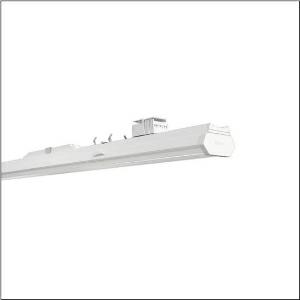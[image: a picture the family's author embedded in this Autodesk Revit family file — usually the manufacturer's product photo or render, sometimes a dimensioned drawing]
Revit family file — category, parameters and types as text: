
# Revit family: licross_r__21_performance_mo_52td16cn445g_c2c6
name_source: partatom
category: Lighting Fixtures
units: mm (PartAtom-declared; Revit-internal decimal feet)

## family parameters
Cut with Voids When Loaded = No
Host = Face
Light Source = No
Part Type = Normal
Room Calculation Point = No
Round Connector Dimension = Use Diameter
Shared = No

## types (1)
- --- (1 x LED, 4500 lm, 24.1 W, 4000K)
    Apparent Load = 24 VA
    CIE Flux Codes = 66 88 96 79 100
    Color Rendering = 80
    Color Temperature = 4000K
    Default Elevation = 1800 mm
    Description = Licross® 21 Performance MO, luminaire insert, of sheet steel, galvanised, coil coated, white, length: 1.500mm, width: 120mm, height: 123mm, LED rated luminous flux: 4.500lm, light colour: 840, control gear: ON/OFF Multilumen, CLOi, control gear: ECG Multilumen, with plug, 3-pole, with phase selection, mains connection: 220..240V, AC, 50/60Hz, halogen-free wiring, primary light control with lens, of plastic, primary optical cover: cover, of PMMA, CAT 2 (L<= 3000cd/m²), light emission: direct/indirect distribution, primary light characteristic: symmetric, protection rating (complete): IP54, insulation class (complete): insulation class I (protective earthing), certification: CE, ENEC, UKCA, protection symbol: D if used in an environment with non-conductive dust loads with corresponding accessories, impact resistance: IK06, permissible ambient temperature for indoor applications: -35..+55°C, corresponds to IFS (International Featured Standards) requirements for safety and quality in the food industry, reducing of maximum allowable ambient temperature of 5°C with ceiling mounting, LABS conformity tested according to VDMA 24364:2018-05, packaging unit: 1 piece
    Height = 114 mm
    Lamp = 1 x LED
    Lamp Light Flux = 4500 lm
    Lamp Power = 24.1 W
    Lamp count = 1
    Length = 1500 mm
    Luminous efficacy = 187 lm/W
    Manufacturer = Siteco
    ModVariant = No
    Model = 52TD16CN445G
    Mounting Place = Ceiling
    Mounting Type = Pendant
    Number of Poles = 1
    OnlyDefault = Yes
    Power Factor = 1
    Product Name = Licross® 21 Performance MO
    Product group = luminaire insert
    ProductGroupID = 902
    Protection Class = Protection class I
    Protection Degree = IP 54
    RLX_Detail_Level = 1
    RlxData = <blob elided: 29313 chars, md5=29c12dba>
    Socket = socket
    Standby Power = 0 W
    System Light Flux = 4500 lm
    System Power = 24 W
    Type Comments = factory setting: luminous flux: 100 % | (A | C | E) | 55 mA
    Type Image = l_1256148.jpg
    URL = http://relux.com
    VarID = @adj_004017
    Voltage = 0 V
    Weight = 0.00 kg
    Width = 120 mm

## geometry (parser evidence)
native form markers: Blend x4, Sweep x12
no freeform markers — native parametric forms only
